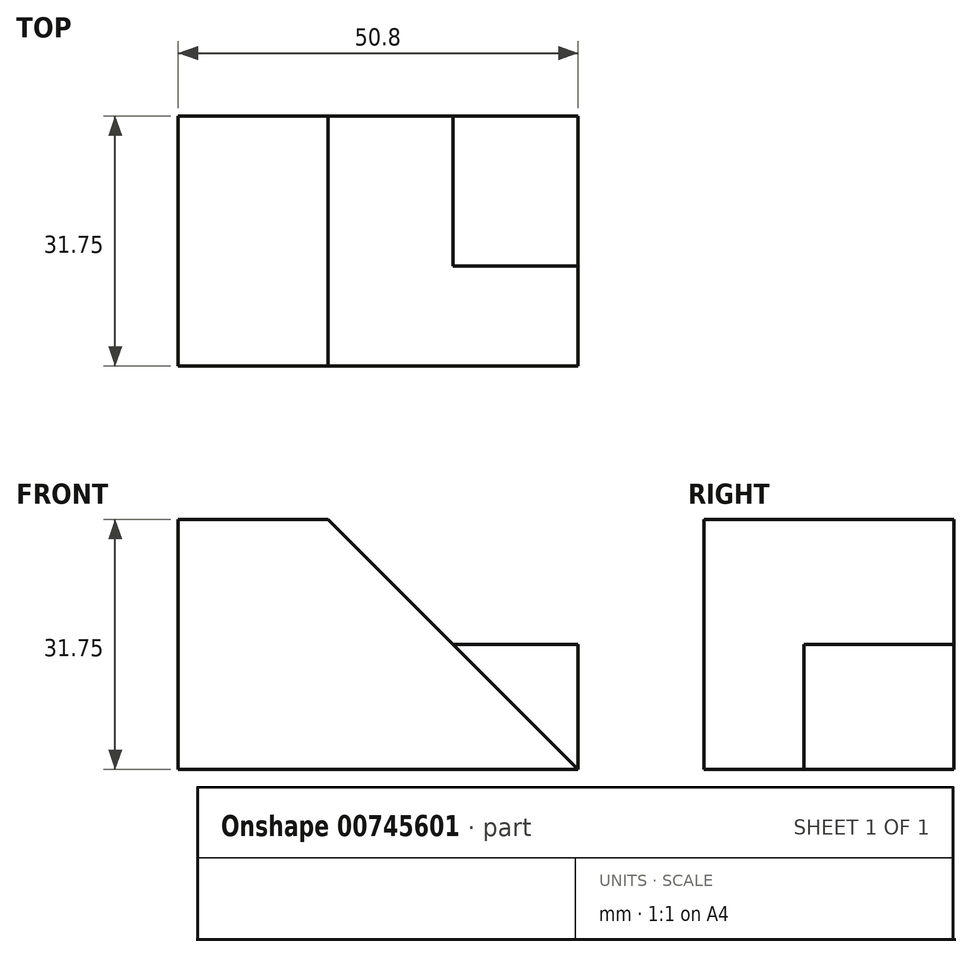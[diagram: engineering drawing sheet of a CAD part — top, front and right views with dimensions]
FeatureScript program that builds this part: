
annotation { "Feature Type Name" : "Feature", "Feature Type Description" : "" }
export const myFeature = defineFeature(function(context is Context, id is Id, definition is map)
    precondition{}
    {
        {
            var Q0;
            Q0=qCreatedBy(makeId("Front.planeOp"),FACE);
            var sketch = newSketch(context, id + "F0", { "sketchPlane" : qUnion([Q0])});
            skLineSegment(sketch, "E0", {"start": v(0, 0) * mm, "end": v(50.8, 0) * mm});
            skLineSegment(sketch, "E1", {"start": v(50.8, 0) * mm, "end": v(50.8, 31.75) * mm});
            skLineSegment(sketch, "E2", {"start": v(50.8, 31.75) * mm, "end": v(0, 31.75) * mm});
            skLineSegment(sketch, "E3", {"start": v(0, 31.75) * mm, "end": v(0, 0) * mm});
            skSolve(sketch);
        }
        {
            var Q0;
            Q0 = qSketchRegion(id + "F0", true);
            extrude(context, id + "F1", {"entities" : qUnion([Q0]), "depth" : 31.75 * mm, "offsetDistance" : 25.4 * mm});
        }
        {
            var Q0;
            Q0=makeQuery(id+"F1.opExtrude","CAP_FACE",FACE,{"disambiguationData":[OSD([sQuery(id+"F0.wireOp",EDGE,"E0"),sQuery(id+"F0.wireOp",EDGE,"E1"),sQuery(id+"F0.wireOp",EDGE,"E2"),sQuery(id+"F0.wireOp",EDGE,"E3")])],"isStart":false});
            var sketch = newSketch(context, id + "F2", { "sketchPlane" : qUnion([Q0])});
            skLineSegment(sketch, "E4", {"start": v(50.8, 0) * mm, "end": v(50.8, 31.75) * mm});
            skLineSegment(sketch, "E5", {"start": v(50.8, 31.75) * mm, "end": v(19.05, 31.75) * mm});
            skLineSegment(sketch, "E6", {"start": v(50.8, 0) * mm, "end": v(19.05, 31.75) * mm});
            skSolve(sketch);
        }
        {
            var Q0;
            Q0=makeQuery(id+"F2.imprint","IMPRINT",FACE,{"disambiguationData":[TD([[makeQuery(id+"F2.imprint","IMPRINT",EDGE,{"derivedFrom":sQuery(id+"F2.wireOp",EDGE,"E4")}),1.0]])]});
            extrude(context, id + "F3", {"entities" : qUnion([Q0]), "operationType" : NewBodyOperationType.REMOVE, "oppositeDirection" : true, "depth" : 12.7 * mm, "offsetDistance" : 25.4 * mm});
        }
        {
            var Q0;
            Q0=makeQuery(id+"F3.boolean.opBoolean","COPY",FACE,{"derivedFrom":makeQuery(id+"F3.opExtrude","CAP_FACE",FACE,{"disambiguationData":[OSD([sQuery(id+"F2.wireOp",EDGE,"E4"),sQuery(id+"F2.wireOp",EDGE,"E5"),sQuery(id+"F2.wireOp",EDGE,"E6")])],"isStart":false})});
            var sketch = newSketch(context, id + "F4", { "sketchPlane" : qUnion([Q0])});
            skLineSegment(sketch, "E7", {"start": v(34.92, 15.88) * mm, "end": v(44.45, 31.75) * mm});
            skLineSegment(sketch, "E8", {"start": v(44.45, 31.75) * mm, "end": v(19.05, 31.75) * mm});
            skLineSegment(sketch, "E9", {"start": v(34.92, 15.88) * mm, "end": v(19.05, 31.75) * mm});
            skSolve(sketch);
        }
        {
            var Q0;
            Q0=makeQuery(id+"F4.imprint","IMPRINT",FACE,{"disambiguationData":[TD([[makeQuery(id+"F4.imprint","IMPRINT",EDGE,{"derivedFrom":sQuery(id+"F4.wireOp",EDGE,"E7")}),1.0]])]});
            extrude(context, id + "F5", {"entities" : qUnion([Q0]), "operationType" : NewBodyOperationType.REMOVE, "oppositeDirection" : true, "depth" : 25.4 * mm, "offsetDistance" : 25.4 * mm});
        }
        {
            var Q0;
            Q0=makeQuery(id+"F3.boolean.opBoolean","COPY",FACE,{"derivedFrom":makeQuery(id+"F3.opExtrude","CAP_FACE",FACE,{"disambiguationData":[OSD([sQuery(id+"F2.wireOp",EDGE,"E4"),sQuery(id+"F2.wireOp",EDGE,"E5"),sQuery(id+"F2.wireOp",EDGE,"E6")])],"isStart":false})});
            var sketch = newSketch(context, id + "F6", { "sketchPlane" : qUnion([Q0])});
            skLineSegment(sketch, "E10", {"start": v(34.92, 15.88) * mm, "end": v(50.8, 19.11) * mm});
            skLineSegment(sketch, "E11", {"start": v(50.8, 19.11) * mm, "end": v(50.8, 31.75) * mm});
            skLineSegment(sketch, "E12", {"start": v(50.8, 31.75) * mm, "end": v(44.45, 31.75) * mm});
            skLineSegment(sketch, "E13", {"start": v(34.92, 15.88) * mm, "end": v(44.45, 31.75) * mm});
            skSolve(sketch);
        }
        {
            var Q0;
            Q0=makeQuery(id+"F6.imprint","IMPRINT",FACE,{"disambiguationData":[TD([[makeQuery(id+"F6.imprint","IMPRINT",EDGE,{"derivedFrom":sQuery(id+"F6.wireOp",EDGE,"E10")}),1.0]])]});
            extrude(context, id + "F7", {"entities" : qUnion([Q0]), "operationType" : NewBodyOperationType.REMOVE, "oppositeDirection" : true, "depth" : 25.4 * mm, "offsetDistance" : 25.4 * mm});
        }
        {
            var Q0;
            Q0=makeQuery(id+"F3.boolean.opBoolean","COPY",FACE,{"derivedFrom":makeQuery(id+"F3.opExtrude","CAP_FACE",FACE,{"disambiguationData":[OSD([sQuery(id+"F2.wireOp",EDGE,"E4"),sQuery(id+"F2.wireOp",EDGE,"E5"),sQuery(id+"F2.wireOp",EDGE,"E6")])],"isStart":false})});
            var sketch = newSketch(context, id + "F8", { "sketchPlane" : qUnion([Q0])});
            skLineSegment(sketch, "E14", {"start": v(34.92, 15.88) * mm, "end": v(50.8, 15.88) * mm});
            skLineSegment(sketch, "E15", {"start": v(50.8, 15.88) * mm, "end": v(50.8, 19.11) * mm});
            skLineSegment(sketch, "E16", {"start": v(50.8, 19.11) * mm, "end": v(34.92, 15.88) * mm});
            skSolve(sketch);
        }
        {
            var Q0;
            Q0=makeQuery(id+"F8.imprint","IMPRINT",FACE,{"disambiguationData":[TD([[makeQuery(id+"F8.imprint","IMPRINT",EDGE,{"derivedFrom":sQuery(id+"F8.wireOp",EDGE,"E14")}),1.0]])]});
            extrude(context, id + "F9", {"entities" : qUnion([Q0]), "operationType" : NewBodyOperationType.REMOVE, "oppositeDirection" : true, "depth" : 25.4 * mm, "offsetDistance" : 25.4 * mm});
        }
    });
